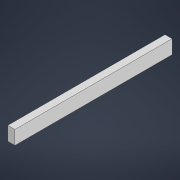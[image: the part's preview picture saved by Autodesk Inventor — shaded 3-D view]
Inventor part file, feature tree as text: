
AUTODESK INVENTOR PART (.ipt)
format: ipt  version: 2022 (Build 260153000, 153)  size: 205,312 bytes
history: native  units: in
note: dims shown in document units (in); Inventor stores cm internally (conversion verified against a paired STEP export)
features: reference x4, other x3, extrude x1, sketch x1
ambient origin geometry x8: Origin, YZ Plane, XZ Plane, XY Plane, X Axis, Y Axis, Z Axis, Center Point
bodies: Solid1 (feature_tree)
feature tree (9):
  extrude  "Extrusion1"  Depth=2.0in TaperAngle=0.0deg
  sketch  "Sketch1"  dims[d0=0.005in d1=2.0in d2=0.0in]
  reference  "Reference1"
  reference  "Reference2"
  reference  "Reference3"
  reference  "Reference4"
  parser-record x1  (decoder bookkeeping rows leaked as tree rows — omitted from the tree; the rows remain in map.json)
  other  "Prototype Assembly.iam"
  other  "Vertical Beam Prototype:1"
note: 1 file-system path scrubbed to <path> (originals preserved in map.json)
